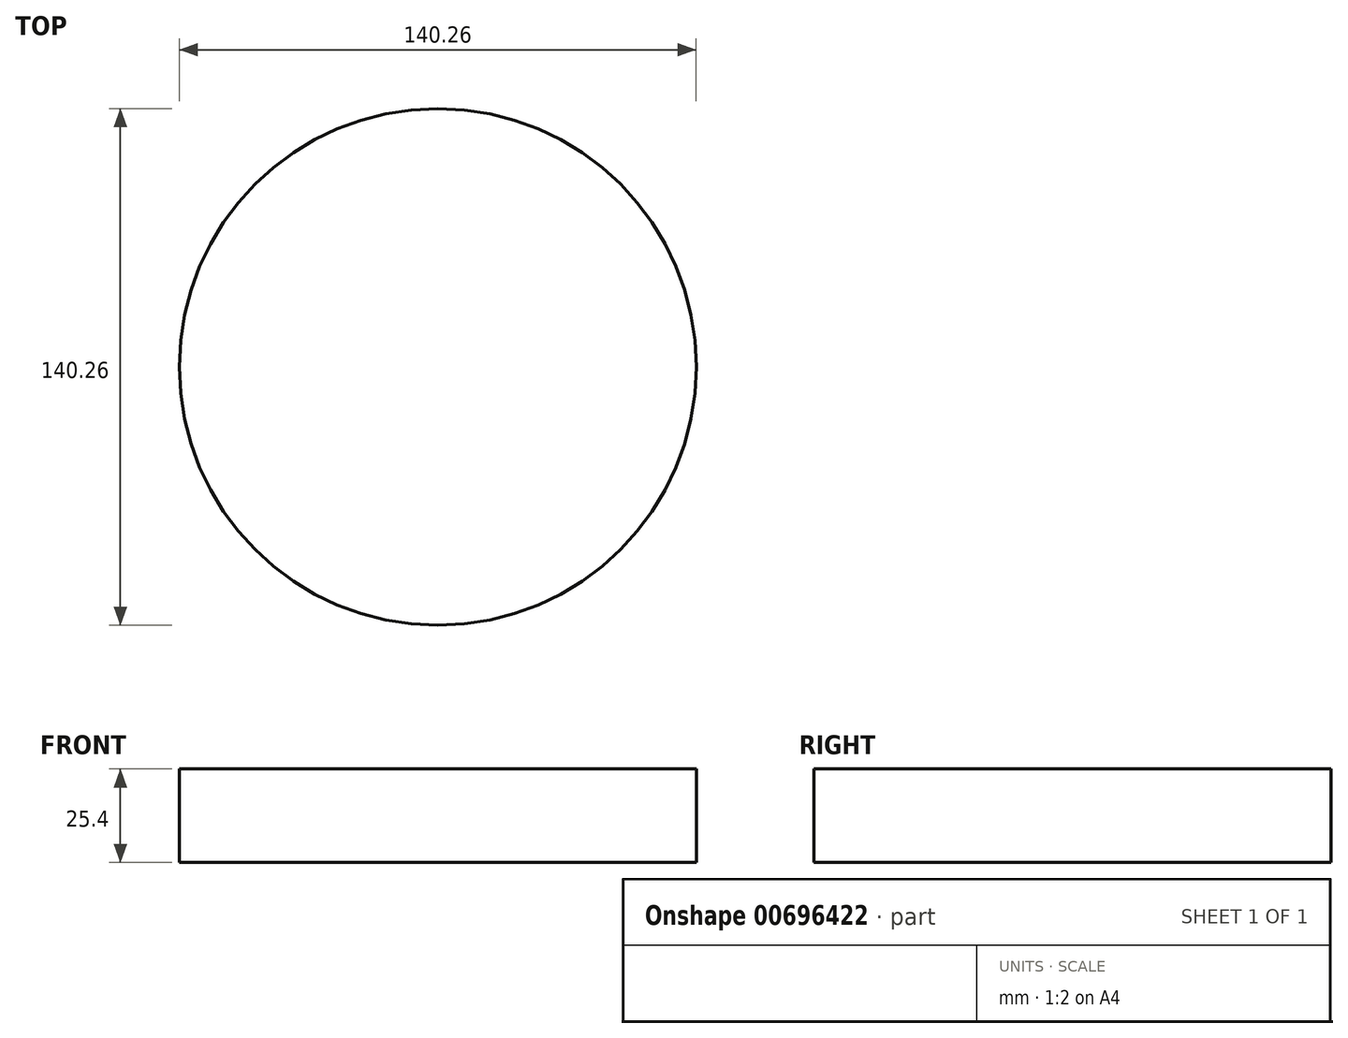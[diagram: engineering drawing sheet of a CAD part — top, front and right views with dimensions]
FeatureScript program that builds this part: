
annotation { "Feature Type Name" : "Feature", "Feature Type Description" : "" }
export const myFeature = defineFeature(function(context is Context, id is Id, definition is map)
    precondition{}
    {
        {
            var Q0;
            Q0=qCreatedBy(makeId("Top.planeOp"),FACE);
            var sketch = newSketch(context, id + "F0", { "sketchPlane" : qUnion([Q0])});
            skCircle(sketch, "E0", {"center": v(0, 0) * mm, "radius": 70.13 * mm});
            skSolve(sketch);
        }
        {
            var Q0;
            Q0=makeQuery(id+"F0.imprint","IMPRINT",FACE,{"disambiguationData":[TD([[makeQuery(id+"F0.imprint","IMPRINT",EDGE,{"derivedFrom":sQuery(id+"F0.wireOp",EDGE,"E0")}),1.0]])]});
            extrude(context, id + "F1", {"entities" : qUnion([Q0]), "depth" : 25.4 * mm, "offsetDistance" : 25.4 * mm});
        }
    });
